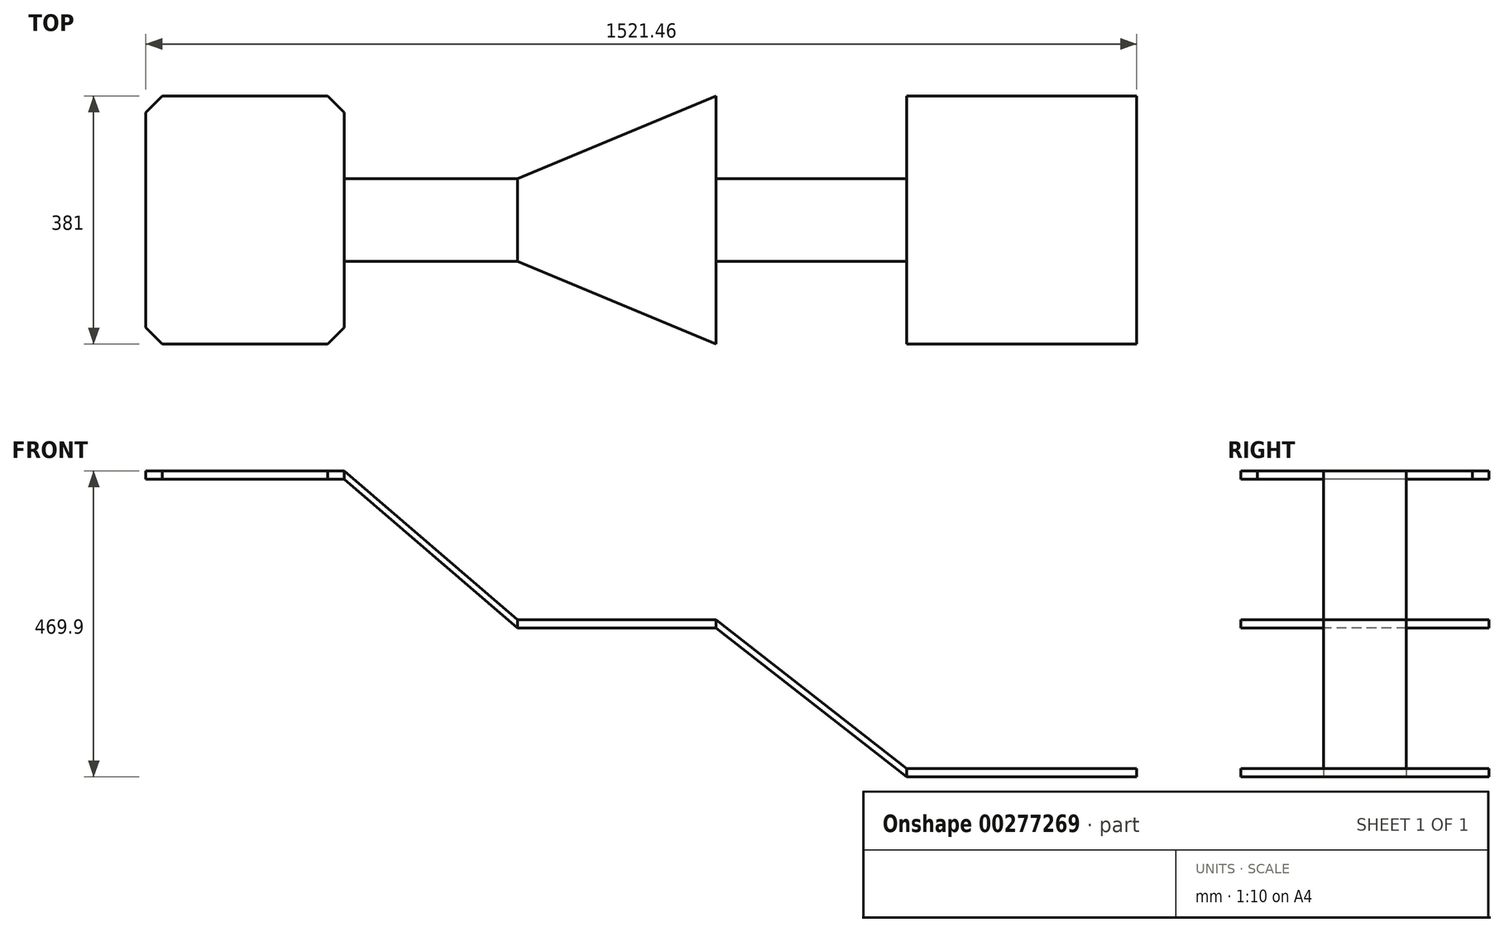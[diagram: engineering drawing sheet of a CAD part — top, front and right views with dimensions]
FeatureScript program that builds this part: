
annotation { "Feature Type Name" : "Feature", "Feature Type Description" : "" }
export const myFeature = defineFeature(function(context is Context, id is Id, definition is map)
    precondition{}
    {
        {
            var Q0;
            Q0=qCreatedBy(makeId("Front.planeOp"),FACE);
            var sketch = newSketch(context, id + "F0", { "sketchPlane" : qUnion([Q0])});
            skLineSegment(sketch, "E0.bottom", {"start": v(762, 228.6) * mm, "end": v(-762, 228.6) * mm, "construction": true});
            skLineSegment(sketch, "E0.top", {"start": v(762, -228.6) * mm, "end": v(-762, -228.6) * mm, "construction": true});
            skLineSegment(sketch, "E0.left", {"start": v(762, 228.6) * mm, "end": v(762, -228.6) * mm, "construction": true});
            skLineSegment(sketch, "E0.right", {"start": v(-762, 228.6) * mm, "end": v(-762, -228.6) * mm, "construction": true});
            skPoint(sketch, "E0.middle", {"position": v(0, 0) * mm});
            skLineSegment(sketch, "E1", {"start": v(-191.38, 0) * mm, "end": v(113.42, 0) * mm});
            skLineSegment(sketch, "E2", {"start": v(113.42, 0) * mm, "end": v(406.4, -228.6) * mm});
            skLineSegment(sketch, "E3", {"start": v(406.4, -228.6) * mm, "end": v(762, -228.6) * mm});
            skLineSegment(sketch, "E4", {"start": v(-457.2, 228.6) * mm, "end": v(-762, 228.6) * mm});
            skLineSegment(sketch, "E5", {"start": v(-457.2, 228.6) * mm, "end": v(-191.38, 0) * mm});
            skSolve(sketch);
        }
        {
            var Q0;
            Q0=sQuery(id+"F0.wireOp",VERTEX,"E4.start");
            var Q1;
            Q1=sQuery(id+"F0.wireOp",EDGE,"E0.bottom");
            cPlane(context, id + "F1", {"entities" : qUnion([Q0, Q1]), "cplaneType" : CPlaneType.LINE_POINT, "offset" : 25.4 * mm, "width" : 152.4 * mm, "height" : 152.4 * mm});
        }
        {
            var Q0;
            Q0=qCreatedBy(id+"F1.planeOp",FACE);
            var sketch = newSketch(context, id + "F2", { "sketchPlane" : qUnion([Q0])});
            skLineSegment(sketch, "E6.bottom", {"start": v(-63.5, 222.25) * mm, "end": v(63.5, 222.25) * mm});
            skLineSegment(sketch, "E6.top", {"start": v(-63.5, 234.95) * mm, "end": v(63.5, 234.95) * mm});
            skLineSegment(sketch, "E6.left", {"start": v(-63.5, 222.25) * mm, "end": v(-63.5, 234.95) * mm});
            skLineSegment(sketch, "E6.right", {"start": v(63.5, 222.25) * mm, "end": v(63.5, 234.95) * mm});
            skPoint(sketch, "E6.middle", {"position": v(0, 228.6) * mm});
            skSolve(sketch);
        }
        {
            var Q0;
            Q0=sQuery(id+"F0.wireOp",VERTEX,"E1.start");
            var Q1;
            Q1=sQuery(id+"F0.wireOp",EDGE,"E0.bottom");
            cPlane(context, id + "F3", {"entities" : qUnion([Q0, Q1]), "cplaneType" : CPlaneType.LINE_POINT, "offset" : 25.4 * mm, "width" : 152.4 * mm, "height" : 152.4 * mm});
        }
        {
            var Q0;
            Q0=qCreatedBy(id+"F3.planeOp",FACE);
            var sketch = newSketch(context, id + "F4", { "sketchPlane" : qUnion([Q0])});
            skLineSegment(sketch, "E7.bottom", {"start": v(-63.5, -6.35) * mm, "end": v(63.5, -6.35) * mm});
            skLineSegment(sketch, "E7.top", {"start": v(-63.5, 6.35) * mm, "end": v(63.5, 6.35) * mm});
            skLineSegment(sketch, "E7.left", {"start": v(-63.5, -6.35) * mm, "end": v(-63.5, 6.35) * mm});
            skLineSegment(sketch, "E7.right", {"start": v(63.5, -6.35) * mm, "end": v(63.5, 6.35) * mm});
            skPoint(sketch, "E7.middle", {"position": v(0, 0) * mm});
            skSolve(sketch);
        }
        {
            var Q0;
            Q0=sQuery(id+"F0.wireOp",VERTEX,"E2.start");
            var Q1;
            Q1=sQuery(id+"F0.wireOp",EDGE,"E0.bottom");
            cPlane(context, id + "F5", {"entities" : qUnion([Q0, Q1]), "cplaneType" : CPlaneType.LINE_POINT, "offset" : 25.4 * mm, "width" : 152.4 * mm, "height" : 152.4 * mm});
        }
        {
            var Q0;
            Q0=qCreatedBy(id+"F5.planeOp",FACE);
            var sketch = newSketch(context, id + "F6", { "sketchPlane" : qUnion([Q0])});
            skLineSegment(sketch, "E8.bottom", {"start": v(190.5, 6.35) * mm, "end": v(-190.5, 6.35) * mm});
            skLineSegment(sketch, "E8.top", {"start": v(190.5, -6.35) * mm, "end": v(-190.5, -6.35) * mm});
            skLineSegment(sketch, "E8.left", {"start": v(190.5, 6.35) * mm, "end": v(190.5, -6.35) * mm});
            skLineSegment(sketch, "E8.right", {"start": v(-190.5, 6.35) * mm, "end": v(-190.5, -6.35) * mm});
            skPoint(sketch, "E8.middle", {"position": v(0, 0) * mm});
            skSolve(sketch);
        }
        {
            var Q0;
            Q0=makeQuery(id+"F2.imprint","IMPRINT",FACE,{"disambiguationData":[TD([[makeQuery(id+"F2.imprint","IMPRINT",EDGE,{"derivedFrom":sQuery(id+"F2.wireOp",EDGE,"E6.bottom")}),1.0]])]});
            var Q1;
            Q1=makeQuery(id+"F4.imprint","IMPRINT",FACE,{"disambiguationData":[TD([[makeQuery(id+"F4.imprint","IMPRINT",EDGE,{"derivedFrom":sQuery(id+"F4.wireOp",EDGE,"E7.bottom")}),1.0]])]});
            loft(context, id + "F7", {"sheetProfilesArray" : [{ "sheetProfileEntities" : qUnion([Q0]) }, { "sheetProfileEntities" : qUnion([Q1]) }]});
        }
        {
            var Q1;
            Q1=makeQuery(id+"F7.opLoft","CAP_FACE",FACE,{"disambiguationData":[OSD([makeQuery(id+"F4.imprint","IMPRINT",FACE,{"disambiguationData":[TD([[makeQuery(id+"F4.imprint","IMPRINT",EDGE,{"derivedFrom":sQuery(id+"F4.wireOp",EDGE,"E7.bottom")}),1.0]])]})])],"isStart":true});
            var Q2;
            Q2=makeQuery(id+"F6.imprint","IMPRINT",FACE,{"disambiguationData":[TD([[makeQuery(id+"F6.imprint","IMPRINT",EDGE,{"derivedFrom":sQuery(id+"F6.wireOp",EDGE,"E8.bottom")}),1.0]])]});
            loft(context, id + "F8", {"operationType" : NewBodyOperationType.ADD, "sheetProfilesArray" : [{ "sheetProfileEntities" : qUnion([Q1]) }, { "sheetProfileEntities" : qUnion([Q2]) }]});
        }
        {
            var Q0;
            Q0=qCreatedBy(id+"F1.planeOp",FACE);
            var sketch = newSketch(context, id + "F9", { "sketchPlane" : qUnion([Q0])});
            skLineSegment(sketch, "E9.bottom", {"start": v(-190.5, 234.95) * mm, "end": v(190.5, 234.95) * mm});
            skLineSegment(sketch, "E9.top", {"start": v(-190.5, 222.25) * mm, "end": v(190.5, 222.25) * mm});
            skLineSegment(sketch, "E9.left", {"start": v(-190.5, 234.95) * mm, "end": v(-190.5, 222.25) * mm});
            skLineSegment(sketch, "E9.right", {"start": v(190.5, 234.95) * mm, "end": v(190.5, 222.25) * mm});
            skPoint(sketch, "E9.middle", {"position": v(0, 228.6) * mm});
            skSolve(sketch);
        }
        {
            var Q0;
            Q0=makeQuery(id+"F9.imprint","IMPRINT",FACE,{"disambiguationData":[TD([[makeQuery(id+"F9.imprint","IMPRINT",EDGE,{"derivedFrom":sQuery(id+"F9.wireOp",EDGE,"E9.bottom")}),-1.0]])]});
            var Q1;
            Q1=sQuery(id+"F0.wireOp",VERTEX,"E4.end");
            extrude(context, id + "F10", {"entities" : qUnion([Q0]), "operationType" : NewBodyOperationType.ADD, "endBound" : BoundingType.UP_TO_VERTEX, "endBoundEntityVertex" : qUnion([Q1]), "depth" : 25.4 * mm});
        }
        {
            var Q0;
            Q0=makeQuery(id+"F10.opExtrude","CAP_EDGE",EDGE,{"disambiguationData":[OSD([sQuery(id+"F9.wireOp",EDGE,"E9.right")])],"isStart":true});
            var Q1;
            Q1=makeQuery(id+"F10.opExtrude","CAP_EDGE",EDGE,{"disambiguationData":[OSD([sQuery(id+"F9.wireOp",EDGE,"E9.right")])],"isStart":false});
            var Q2;
            Q2=makeQuery(id+"F10.opExtrude","CAP_EDGE",EDGE,{"disambiguationData":[OSD([sQuery(id+"F9.wireOp",EDGE,"E9.left")])],"isStart":true});
            var Q3;
            Q3=makeQuery(id+"F10.opExtrude","CAP_EDGE",EDGE,{"disambiguationData":[OSD([sQuery(id+"F9.wireOp",EDGE,"E9.left")])],"isStart":false});
            chamfer(context, id + "F11", {"entities" : qUnion([Q0, Q1, Q2, Q3]), "width" : 25.4 * mm, "tangentPropagation" : true});
        }
        {
            var Q0;
            Q0=sQuery(id+"F0.wireOp",VERTEX,"E3.start");
            var Q1;
            Q1=sQuery(id+"F0.wireOp",EDGE,"E3");
            cPlane(context, id + "F12", {"entities" : qUnion([Q0, Q1]), "cplaneType" : CPlaneType.LINE_POINT, "offset" : 25.4 * mm, "width" : 152.4 * mm, "height" : 152.4 * mm});
        }
        {
            var Q0;
            Q0=qCreatedBy(id+"F12.planeOp",FACE);
            var sketch = newSketch(context, id + "F13", { "sketchPlane" : qUnion([Q0])});
            skLineSegment(sketch, "E10.bottom", {"start": v(63.5, -222.25) * mm, "end": v(-63.5, -222.25) * mm});
            skLineSegment(sketch, "E10.top", {"start": v(63.5, -234.95) * mm, "end": v(-63.5, -234.95) * mm});
            skLineSegment(sketch, "E10.left", {"start": v(63.5, -222.25) * mm, "end": v(63.5, -234.95) * mm});
            skLineSegment(sketch, "E10.right", {"start": v(-63.5, -222.25) * mm, "end": v(-63.5, -234.95) * mm});
            skPoint(sketch, "E10.middle", {"position": v(0, -228.6) * mm});
            skSolve(sketch);
        }
        {
            var Q0;
            Q0=makeQuery(id+"F13.imprint","IMPRINT",FACE,{"disambiguationData":[TD([[makeQuery(id+"F13.imprint","IMPRINT",EDGE,{"derivedFrom":sQuery(id+"F13.wireOp",EDGE,"E10.bottom")}),1.0]])]});
            var Q1;
            Q1=sQuery(id+"F0.wireOp",EDGE,"E2");
            sweep(context, id + "F14", {"operationType" : NewBodyOperationType.ADD, "profiles" : qUnion([Q0]), "path" : qUnion([Q1])});
        }
        {
            var Q0;
            Q0=qCreatedBy(id+"F12.planeOp",FACE);
            var sketch = newSketch(context, id + "F15", { "sketchPlane" : qUnion([Q0])});
            skLineSegment(sketch, "E11.bottom", {"start": v(190.5, -222.25) * mm, "end": v(-190.5, -222.25) * mm});
            skLineSegment(sketch, "E11.top", {"start": v(190.5, -234.95) * mm, "end": v(-190.5, -234.95) * mm});
            skLineSegment(sketch, "E11.left", {"start": v(190.5, -222.25) * mm, "end": v(190.5, -234.95) * mm});
            skLineSegment(sketch, "E11.right", {"start": v(-190.5, -222.25) * mm, "end": v(-190.5, -234.95) * mm});
            skPoint(sketch, "E11.middle", {"position": v(0, -228.6) * mm});
            skSolve(sketch);
        }
        {
            var Q0;
            Q0=makeQuery(id+"F15.imprint","IMPRINT",FACE,{"disambiguationData":[TD([[makeQuery(id+"F15.imprint","IMPRINT",EDGE,{"derivedFrom":sQuery(id+"F15.wireOp",EDGE,"E11.bottom")}),1.0]])]});
            extrude(context, id + "F16", {"entities" : qUnion([Q0]), "operationType" : NewBodyOperationType.ADD, "depth" : 353.06 * mm});
        }
    });
